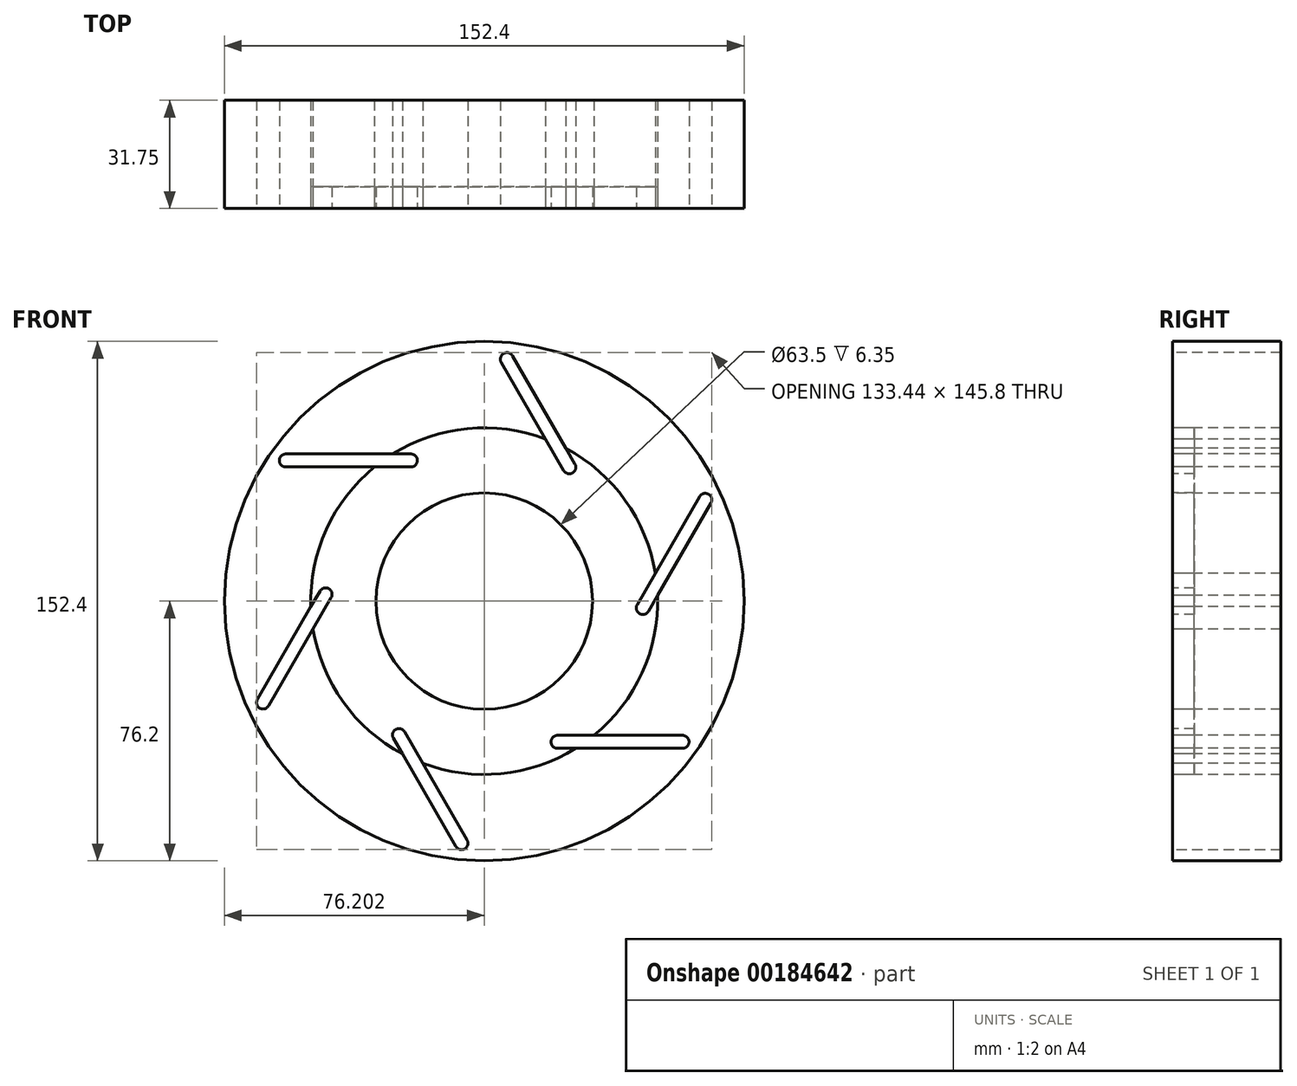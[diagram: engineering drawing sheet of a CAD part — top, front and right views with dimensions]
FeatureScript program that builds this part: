
annotation { "Feature Type Name" : "Feature", "Feature Type Description" : "" }
export const myFeature = defineFeature(function(context is Context, id is Id, definition is map)
    precondition{}
    {
        {
            var Q0;
            Q0=qCreatedBy(makeId("Front.planeOp"),FACE);
            var sketch = newSketch(context, id + "F0", { "sketchPlane" : qUnion([Q0])});
            skCircle(sketch, "E0", {"center": v(14.87, 6.4) * mm, "radius": 31.75 * mm});
            skPoint(sketch, "E1", {"position": v(-31.63, 8.41) * mm});
            skPoint(sketch, "E2", {"position": v(-10.12, -32.86) * mm});
            skPoint(sketch, "E3", {"position": v(36.38, -34.87) * mm});
            skPoint(sketch, "E4", {"position": v(61.37, 4.39) * mm});
            skPoint(sketch, "E5", {"position": v(39.86, 45.66) * mm});
            skPoint(sketch, "E6", {"position": v(-6.63, 47.68) * mm});
            skCircle(sketch, "E7", {"center": v(14.87, 6.4) * mm, "radius": 50.84 * mm});
            skCircle(sketch, "E8", {"center": v(14.87, 6.4) * mm, "radius": 74.5 * mm});
            skCircle(sketch, "E9", {"center": v(14.87, 6.4) * mm, "radius": 76.2 * mm});
            skArc(sketch, "E10", {"start": v(38.21, 44.7) * mm, "mid": v(40.82, 44.01) * mm, "end": v(41.51, 46.61) * mm});
            skArc(sketch, "E11", {"start": v(23.18, 78.36) * mm, "mid": v(20.58, 79.06) * mm, "end": v(19.88, 76.46) * mm});
            skArc(sketch, "E12", {"start": v(-43.3, 49.58) * mm, "mid": v(-45.2, 47.68) * mm, "end": v(-43.3, 45.77) * mm});
            skArc(sketch, "E13", {"start": v(-6.63, 45.77) * mm, "mid": v(-4.73, 47.68) * mm, "end": v(-6.63, 49.58) * mm});
            skArc(sketch, "E14", {"start": v(-29.98, 7.46) * mm, "mid": v(-30.67, 10.06) * mm, "end": v(-33.28, 9.37) * mm});
            skArc(sketch, "E15", {"start": v(-51.6, -22.38) * mm, "mid": v(-50.9, -24.99) * mm, "end": v(-48.3, -24.29) * mm});
            skArc(sketch, "E16", {"start": v(-8.47, -31.9) * mm, "mid": v(-11.07, -31.21) * mm, "end": v(-11.77, -33.81) * mm});
            skArc(sketch, "E17", {"start": v(6.56, -65.56) * mm, "mid": v(9.16, -66.26) * mm, "end": v(9.86, -63.66) * mm});
            skArc(sketch, "E18", {"start": v(36.38, -32.97) * mm, "mid": v(34.47, -34.87) * mm, "end": v(36.38, -36.78) * mm});
            skArc(sketch, "E19", {"start": v(73.04, -36.78) * mm, "mid": v(74.94, -34.87) * mm, "end": v(73.04, -32.97) * mm});
            skArc(sketch, "E20", {"start": v(59.72, 5.34) * mm, "mid": v(60.42, 2.74) * mm, "end": v(63.02, 3.43) * mm});
            skArc(sketch, "E21", {"start": v(81.35, 35.18) * mm, "mid": v(80.65, 37.79) * mm, "end": v(78.05, 37.09) * mm});
            skLineSegment(sketch, "E22", {"start": v(78.05, 37.09) * mm, "end": v(59.72, 5.34) * mm});
            skLineSegment(sketch, "E23", {"start": v(63.02, 3.43) * mm, "end": v(81.35, 35.18) * mm});
            skLineSegment(sketch, "E24", {"start": v(41.51, 46.61) * mm, "end": v(23.18, 78.36) * mm});
            skLineSegment(sketch, "E25", {"start": v(19.88, 76.46) * mm, "end": v(38.21, 44.7) * mm});
            skLineSegment(sketch, "E26", {"start": v(-6.63, 49.58) * mm, "end": v(-43.3, 49.58) * mm});
            skLineSegment(sketch, "E27", {"start": v(-43.3, 45.77) * mm, "end": v(-6.63, 45.77) * mm});
            skLineSegment(sketch, "E28", {"start": v(-33.28, 9.37) * mm, "end": v(-51.6, -22.38) * mm});
            skLineSegment(sketch, "E29", {"start": v(-48.3, -24.29) * mm, "end": v(-29.98, 7.46) * mm});
            skLineSegment(sketch, "E30", {"start": v(-8.47, -31.9) * mm, "end": v(9.86, -63.66) * mm});
            skLineSegment(sketch, "E31", {"start": v(6.56, -65.56) * mm, "end": v(-11.77, -33.81) * mm});
            skLineSegment(sketch, "E32", {"start": v(36.38, -36.78) * mm, "end": v(73.04, -36.78) * mm});
            skLineSegment(sketch, "E33", {"start": v(73.04, -32.97) * mm, "end": v(36.38, -32.97) * mm});
            skPoint(sketch, "E34", {"position": v(36.25, 52.53) * mm});
            skSolve(sketch);
        }
        {
            var Q0;
            Q0=makeQuery(id+"F0.imprint","IMPRINT",FACE,{"disambiguationData":[TD([[makeQuery(id+"F0.imprint","IMPRINT",EDGE,{"derivedFrom":sQuery(id+"F0.wireOp",EDGE,"E0")}),-1.0]])]});
            extrude(context, id + "F1", {"entities" : qUnion([Q0]), "oppositeDirection" : true, "depth" : 6.35 * mm});
        }
        {
            var Q0;
            {var subQ1=sQuery(id+"F0.wireOp",EDGE,"bX90t1Dk-m4s5-3UPS-Sgd3-fSBXpBS4URNl");var subQ9=sQuery(id+"F0.wireOp",EDGE,"TgSIVYeb-09Fl-svnb-8OfH-n3cuDx7MIz0P");var subQ11=makeQuery(id+"F0.imprint","INTERSECT",VERTEX,{"derivedFrom":[subQ1,subQ9]});Q0=makeQuery(id+"F0.imprint","IMPRINT",FACE,{"disambiguationData":[TD([[makeQuery(id+"F0.imprint","IMPRINT",EDGE,{"disambiguationData":[TD([[subQ11,1.0]])],"derivedFrom":subQ1}),-1.0]])]});}
            var Q1;
            {var subQ1=sQuery(id+"F0.wireOp",EDGE,"C24nEaDh-JLNN-c9Xw-QU1O-adHOCJCjBXYC");var subQ8=sQuery(id+"F0.wireOp",EDGE,"vhxadlnU-t8PW-Mbpp-0GBU-7rwsZVoTwnvr");var subQ11=makeQuery(id+"F0.imprint","INTERSECT",VERTEX,{"derivedFrom":[subQ1,subQ8]});Q1=makeQuery(id+"F0.imprint","IMPRINT",FACE,{"disambiguationData":[TD([[makeQuery(id+"F0.imprint","IMPRINT",EDGE,{"disambiguationData":[TD([[subQ11,-1.0]])],"derivedFrom":subQ1}),-1.0]])]});}
            var Q2;
            {var subQ1=sQuery(id+"F0.wireOp",EDGE,"C24nEaDh-JLNN-c9Xw-QU1O-adHOCJCjBXYC");var subQ5=sQuery(id+"F0.wireOp",EDGE,"HmoioYX4-HWMN-eaA3-MHM3-Xqdy5ffKxehf");var subQ11=makeQuery(id+"F0.imprint","INTERSECT",VERTEX,{"derivedFrom":[subQ1,subQ5]});Q2=makeQuery(id+"F0.imprint","IMPRINT",FACE,{"disambiguationData":[TD([[makeQuery(id+"F0.imprint","IMPRINT",EDGE,{"disambiguationData":[TD([[subQ11,1.0]])],"derivedFrom":subQ1}),-1.0]])]});}
            var Q3;
            {var subQ1=sQuery(id+"F0.wireOp",EDGE,"73VJwdmQ-1ihY-OQjm-pAyM-CmCK1jExDeSG");var subQ7=sQuery(id+"F0.wireOp",EDGE,"jll4ODov-3mgA-5HwD-mLFM-dlqajUard0VY");var subQ11=makeQuery(id+"F0.imprint","INTERSECT",VERTEX,{"derivedFrom":[subQ1,subQ7]});Q3=makeQuery(id+"F0.imprint","IMPRINT",FACE,{"disambiguationData":[TD([[makeQuery(id+"F0.imprint","IMPRINT",EDGE,{"disambiguationData":[TD([[subQ11,1.0]])],"derivedFrom":subQ1}),-1.0]])]});}
            var Q4;
            {var subQ1=sQuery(id+"F0.wireOp",EDGE,"60yEr6lX-O2ea-3m5o-jAWv-VT3wAf2MRhvl");var subQ5=sQuery(id+"F0.wireOp",EDGE,"tf2vaDBH-RUl0-01ll-vlCh-kbP6NbKI7VAh");var subQ11=makeQuery(id+"F0.imprint","INTERSECT",VERTEX,{"derivedFrom":[subQ1,subQ5]});Q4=makeQuery(id+"F0.imprint","IMPRINT",FACE,{"disambiguationData":[TD([[makeQuery(id+"F0.imprint","IMPRINT",EDGE,{"disambiguationData":[TD([[subQ11,1.0]])],"derivedFrom":subQ1}),-1.0]])]});}
            var Q5;
            {var subQ1=sQuery(id+"F0.wireOp",EDGE,"K8E4rF5M-OpdS-LXBm-Na9K-qDIkHJus2A65");var subQ5=sQuery(id+"F0.wireOp",EDGE,"7tO7Gvpt-nAfb-GQrI-Bw1T-2U5OcgDE15wG");var subQ11=makeQuery(id+"F0.imprint","INTERSECT",VERTEX,{"derivedFrom":[subQ1,subQ5]});Q5=makeQuery(id+"F0.imprint","IMPRINT",FACE,{"disambiguationData":[TD([[makeQuery(id+"F0.imprint","IMPRINT",EDGE,{"disambiguationData":[TD([[subQ11,1.0]])],"derivedFrom":subQ1}),-1.0]])]});}
            var Q6;
            Q6=makeQuery(id+"F0.imprint","IMPRINT",FACE,{"disambiguationData":[TD([[makeQuery(id+"F0.imprint","IMPRINT",EDGE,{"derivedFrom":sQuery(id+"F0.wireOp",EDGE,"E9")}),1.0]])]});
            var Q7;
            Q7=makeQuery(id+"F0.imprint","IMPRINT",FACE,{"disambiguationData":[TD([[makeQuery(id+"F0.imprint","IMPRINT",EDGE,{"derivedFrom":sQuery(id+"F0.wireOp",EDGE,"E8")}),1.0]])]});
            extrude(context, id + "F2", {"entities" : qUnion([Q0, Q1, Q2, Q3, Q4, Q5, Q6, Q7]), "oppositeDirection" : true, "depth" : 31.75 * mm});
        }
    });
